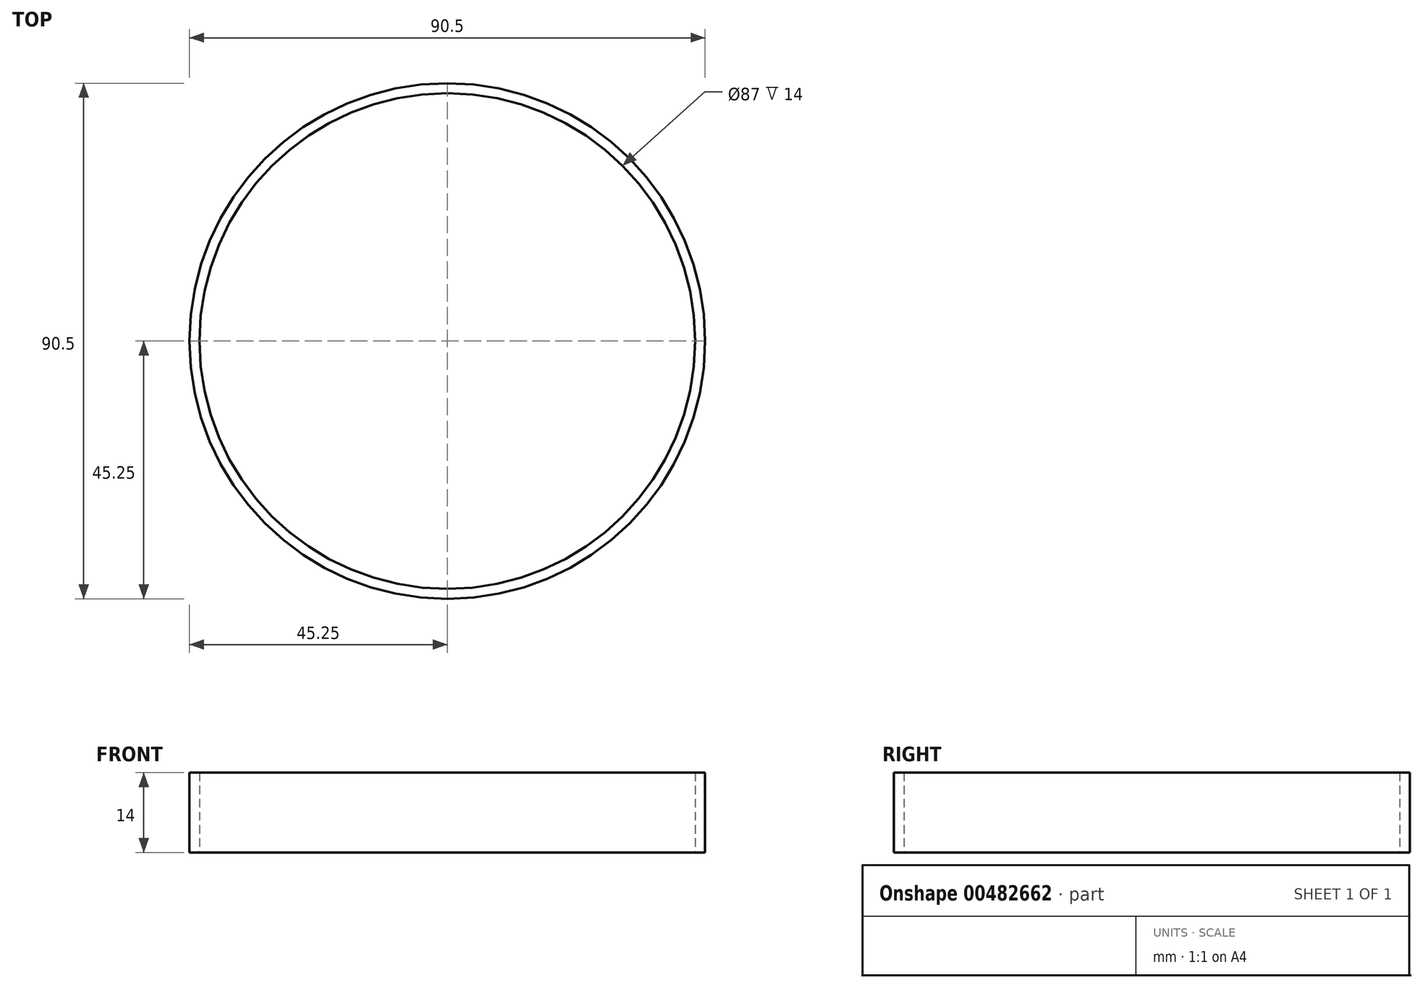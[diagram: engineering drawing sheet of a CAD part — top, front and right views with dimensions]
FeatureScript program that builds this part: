
annotation { "Feature Type Name" : "Feature", "Feature Type Description" : "" }
export const myFeature = defineFeature(function(context is Context, id is Id, definition is map)
    precondition{}
    {
        {
            var Q0;
            Q0=qCreatedBy(makeId("Top.planeOp"),FACE);
            var sketch = newSketch(context, id + "F0", { "sketchPlane" : qUnion([Q0])});
            skCircle(sketch, "E0", {"center": v(0, 0) * mm, "radius": 43.5 * mm});
            skCircle(sketch, "E1", {"center": v(0, 0) * mm, "radius": 45.25 * mm});
            skSolve(sketch);
        }
        {
            var Q0;
            Q0 = qSketchRegion(id + "F0", true);
            extrude(context, id + "F1", {"entities" : qUnion([Q0]), "depth" : 14 * mm});
        }
    });
